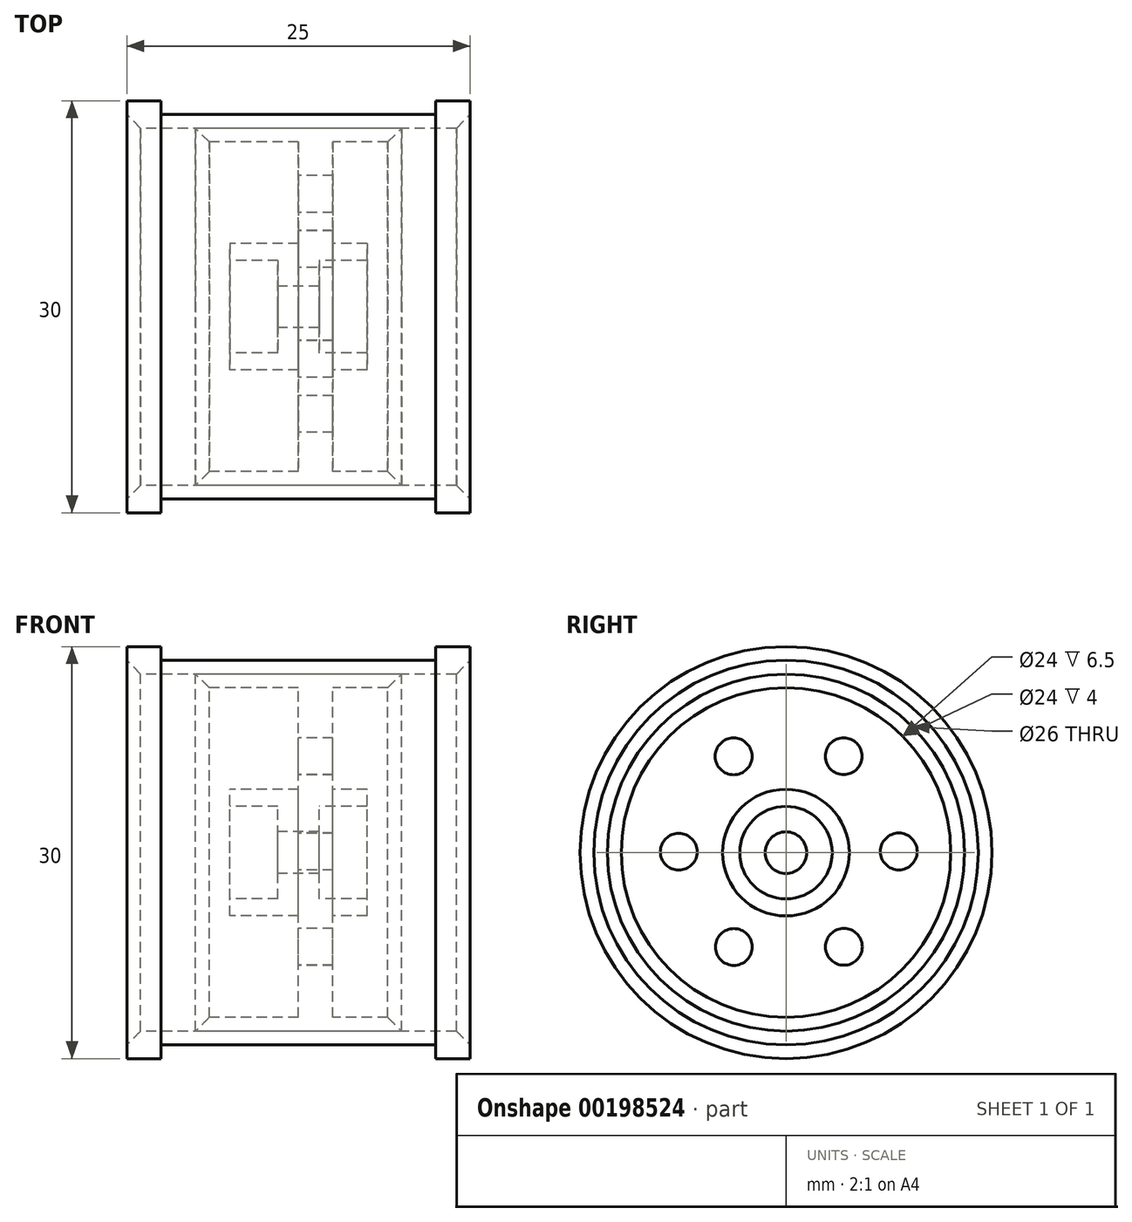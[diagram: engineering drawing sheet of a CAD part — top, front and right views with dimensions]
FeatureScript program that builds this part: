
annotation { "Feature Type Name" : "Feature", "Feature Type Description" : "" }
export const myFeature = defineFeature(function(context is Context, id is Id, definition is map)
    precondition{}
    {
        {
            var Q0;
            Q0=qCreatedBy(makeId("Right.planeOp"),FACE);
            var sketch = newSketch(context, id + "F0", { "sketchPlane" : qUnion([Q0])});
            skCircle(sketch, "E0", {"center": v(0, 0) * mm, "radius": 15 * mm});
            skCircle(sketch, "E1", {"center": v(0, 0) * mm, "radius": 13 * mm});
            skCircle(sketch, "E2", {"center": v(0, 0) * mm, "radius": 12 * mm});
            skCircle(sketch, "E3", {"center": v(0, 0) * mm, "radius": 4.61 * mm});
            skCircle(sketch, "E4", {"center": v(0, 0) * mm, "radius": 3.37 * mm});
            skCircle(sketch, "E5", {"center": v(0, 0) * mm, "radius": 1.51 * mm});
            skLineSegment(sketch, "E6", {"start": v(-6, -10.4) * mm, "end": v(6.7, 9.96) * mm, "construction": true});
            skCircle(sketch, "E7", {"center": v(-3.8, -6.87) * mm, "radius": 1.34 * mm});
            skCircle(sketch, "E8.1.0", {"center": v(4.22, -6.86) * mm, "radius": 1.34 * mm});
            skCircle(sketch, "E8.2.0", {"center": v(8.22, 0.08) * mm, "radius": 1.34 * mm});
            skCircle(sketch, "E8.3.0", {"center": v(4.2, 7.02) * mm, "radius": 1.34 * mm});
            skCircle(sketch, "E8.4.0", {"center": v(-3.81, 7) * mm, "radius": 1.34 * mm});
            skCircle(sketch, "E8.5.0", {"center": v(-7.8, 0.06) * mm, "radius": 1.34 * mm});
            skPoint(sketch, "E8.center", {"position": v(0.2, 0.07) * mm});
            skCircle(sketch, "E9", {"center": v(0, 0) * mm, "radius": 14 * mm});
            skSolve(sketch);
        }
        {
            var Q0;
            Q0=makeQuery(id+"F0.imprint","IMPRINT",FACE,{"disambiguationData":[TD([[makeQuery(id+"F0.imprint","IMPRINT",EDGE,{"derivedFrom":sQuery(id+"F0.wireOp",EDGE,"E0")}),1.0]])]});
            var Q1;
            Q1=makeQuery(id+"F0.imprint","IMPRINT",FACE,{"disambiguationData":[TD([[makeQuery(id+"F0.imprint","IMPRINT",EDGE,{"derivedFrom":sQuery(id+"F0.wireOp",EDGE,"E1")}),-1.0]])]});
            extrude(context, id + "F1", {"entities" : qUnion([Q0, Q1]), "endBound" : BoundingType.SYMMETRIC, "depth" : 25 * mm});
        }
        {
            var Q0;
            Q0=makeQuery(id+"F0.imprint","IMPRINT",FACE,{"disambiguationData":[TD([[makeQuery(id+"F0.imprint","IMPRINT",EDGE,{"derivedFrom":sQuery(id+"F0.wireOp",EDGE,"E1")}),1.0]])]});
            var Q1;
            Q1=sQuery(id+"F0.wireOp",EDGE,"E2");
            var Q2;
            Q2=sQuery(id+"F0.wireOp",EDGE,"E1");
            extrude(context, id + "F2", {"entities" : qUnion([Q0]), "surfaceEntities" : qUnion([Q1, Q2]), "endBound" : BoundingType.SYMMETRIC, "depth" : 15 * mm});
        }
        {
            var Q0;
            Q0=makeQuery(id+"F0.imprint","IMPRINT",FACE,{"disambiguationData":[TD([[makeQuery(id+"F0.imprint","IMPRINT",EDGE,{"derivedFrom":sQuery(id+"F0.wireOp",EDGE,"E2")}),1.0]])]});
            extrude(context, id + "F3", {"entities" : qUnion([Q0]), "operationType" : NewBodyOperationType.ADD, "depth" : 2.5 * mm});
        }
        {
            var Q0;
            Q0=makeQuery(id+"F0.imprint","IMPRINT",FACE,{"disambiguationData":[TD([[makeQuery(id+"F0.imprint","IMPRINT",EDGE,{"derivedFrom":sQuery(id+"F0.wireOp",EDGE,"E3")}),1.0]])]});
            extrude(context, id + "F4", {"entities" : qUnion([Q0]), "operationType" : NewBodyOperationType.ADD, "endBound" : BoundingType.SYMMETRIC, "depth" : 10 * mm});
        }
        {
            var Q0;
            Q0=makeQuery(id+"F0.imprint","IMPRINT",FACE,{"disambiguationData":[TD([[makeQuery(id+"F0.imprint","IMPRINT",EDGE,{"derivedFrom":sQuery(id+"F0.wireOp",EDGE,"E4")}),1.0]])]});
            extrude(context, id + "F5", {"entities" : qUnion([Q0]), "operationType" : NewBodyOperationType.ADD, "endBound" : BoundingType.SYMMETRIC, "depth" : 3 * mm});
        }
        {
            var Q0;
            Q0=makeQuery(id+"F0.imprint","IMPRINT",FACE,{"disambiguationData":[TD([[makeQuery(id+"F0.imprint","IMPRINT",EDGE,{"derivedFrom":sQuery(id+"F0.wireOp",EDGE,"E0")}),1.0]])]});
            extrude(context, id + "F6", {"entities" : qUnion([Q0]), "operationType" : NewBodyOperationType.REMOVE, "endBound" : BoundingType.SYMMETRIC, "oppositeDirection" : true, "depth" : 20 * mm});
        }
        {
            var Q0;
            Q0=makeQuery(id+"F2.opExtrude","CAP_EDGE",EDGE,{"disambiguationData":[OSD([sQuery(id+"F0.wireOp",EDGE,"E2")])],"isStart":false});
            var Q1;
            Q1=makeQuery(id+"F2.opExtrude","CAP_EDGE",EDGE,{"disambiguationData":[OSD([sQuery(id+"F0.wireOp",EDGE,"E2")])],"isStart":true});
            chamfer(context, id + "F7", {"entities" : qUnion([Q0, Q1]), "width" : 1 * mm, "tangentPropagation" : true});
        }
        {
            var Q0;
            Q0=makeQuery(id+"F1.opExtrude","CAP_EDGE",EDGE,{"disambiguationData":[OSD([sQuery(id+"F0.wireOp",EDGE,"E1")])],"isStart":true});
            var Q1;
            Q1=makeQuery(id+"F1.opExtrude","CAP_EDGE",EDGE,{"disambiguationData":[OSD([sQuery(id+"F0.wireOp",EDGE,"E1")])],"isStart":false});
            chamfer(context, id + "F8", {"entities" : qUnion([Q0, Q1]), "width" : 1 * mm, "tangentPropagation" : true});
        }
    });
